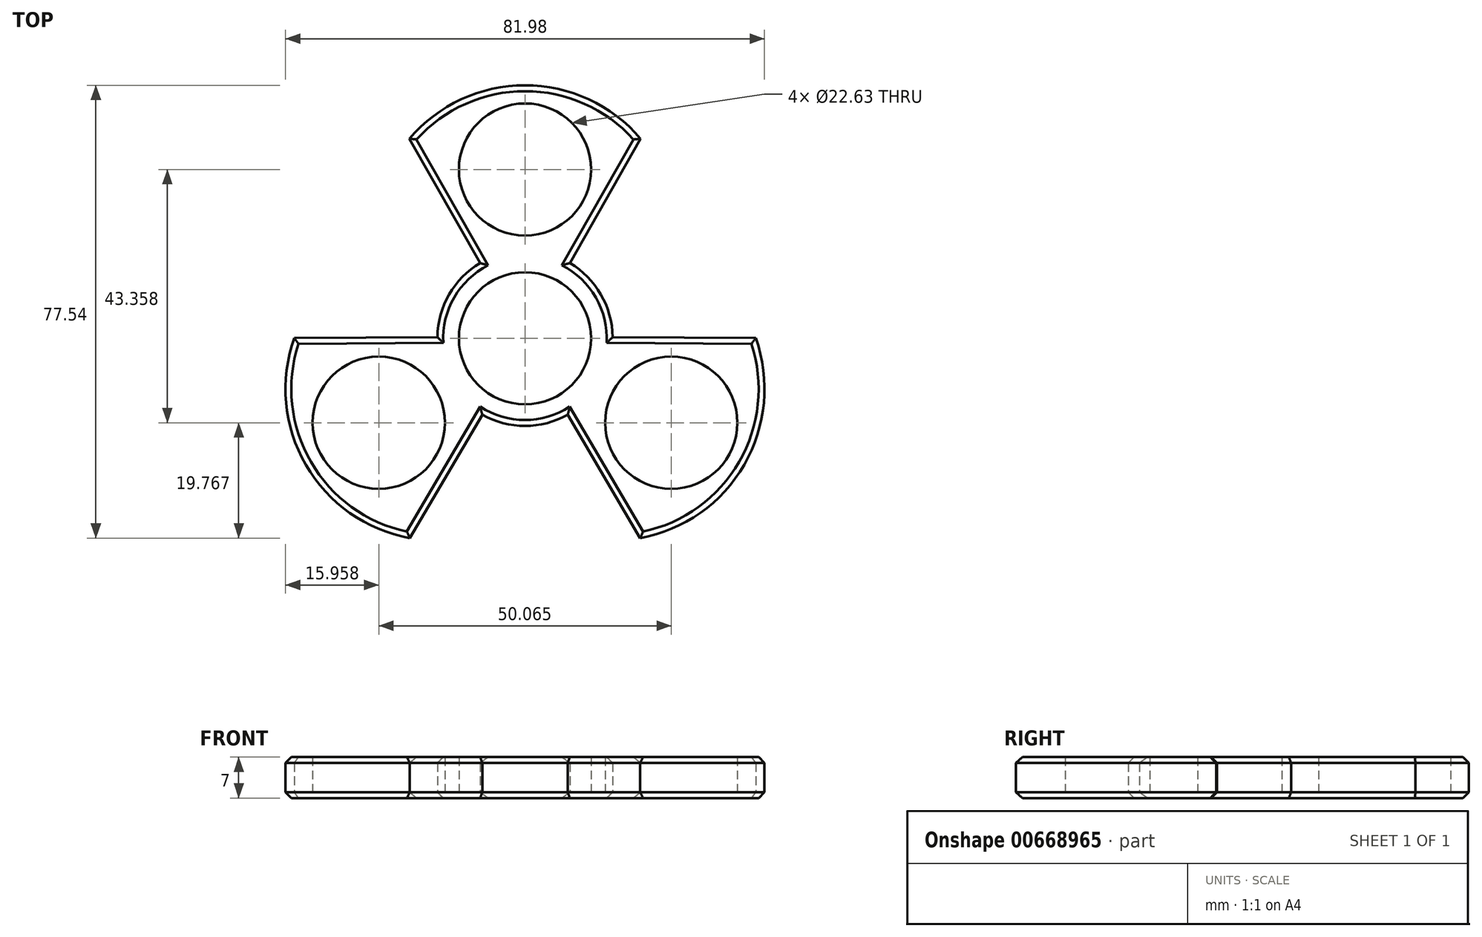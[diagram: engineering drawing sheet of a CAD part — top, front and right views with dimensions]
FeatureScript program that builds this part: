
annotation { "Feature Type Name" : "Feature", "Feature Type Description" : "" }
export const myFeature = defineFeature(function(context is Context, id is Id, definition is map)
    precondition{}
    {
        {
            var Q0;
            Q0=qCreatedBy(makeId("Top.planeOp"),FACE);
            var sketch = newSketch(context, id + "F0", { "sketchPlane" : qUnion([Q0])});
            skCircle(sketch, "E0", {"center": v(0, 0) * mm, "radius": 11.32 * mm});
            skCircle(sketch, "E1", {"center": v(0, 0) * mm, "radius": 45 * mm, "construction": true});
            skCircle(sketch, "E2", {"center": v(0, 0) * mm, "radius": 15 * mm});
            skLineSegment(sketch, "E3", {"start": v(-7.69, 12.88) * mm, "end": v(-19.78, 34.18) * mm});
            skLineSegment(sketch, "E4.MirrorCS", {"start": v(7.69, 12.88) * mm, "end": v(19.78, 34.18) * mm});
            skArc(sketch, "E5", {"start": v(19.78, 34.18) * mm, "mid": v(0, 43.32) * mm, "end": v(-19.78, 34.18) * mm});
            skCircle(sketch, "E6", {"center": v(0, 28.9) * mm, "radius": 11.32 * mm});
            skLineSegment(sketch, "E7.1.0", {"start": v(-7.31, -13.1) * mm, "end": v(-19.7, -34.22) * mm});
            skArc(sketch, "E7.1.1", {"start": v(-39.49, 0.05) * mm, "mid": v(-37.51, -21.66) * mm, "end": v(-19.7, -34.22) * mm});
            skCircle(sketch, "E7.1.2", {"center": v(-25.03, -14.45) * mm, "radius": 11.32 * mm});
            skLineSegment(sketch, "E7.1.3", {"start": v(-15, 0.22) * mm, "end": v(-39.49, 0.05) * mm});
            skLineSegment(sketch, "E7.2.0", {"start": v(15, 0.22) * mm, "end": v(39.49, 0.05) * mm});
            skArc(sketch, "E7.2.1", {"start": v(19.7, -34.22) * mm, "mid": v(37.51, -21.66) * mm, "end": v(39.49, 0.05) * mm});
            skCircle(sketch, "E7.2.2", {"center": v(25.03, -14.45) * mm, "radius": 11.32 * mm});
            skLineSegment(sketch, "E7.2.3", {"start": v(7.31, -13.1) * mm, "end": v(19.7, -34.22) * mm});
            skSolve(sketch);
        }
        {
            var Q0;
            Q0 = qSketchRegion(id + "F0", true);
            extrude(context, id + "F1", {"entities" : qUnion([Q0]), "depth" : 7 * mm, "offsetDistance" : 25 * mm});
        }
        {
            var Q0;
            Q0=makeQuery(id+"F1.opExtrude","CAP_EDGE",EDGE,{"disambiguationData":[OSD([sQuery(id+"F0.wireOp",EDGE,"E7.1.3")])],"isStart":false});
            var Q1;
            Q1=makeQuery(id+"F1.opExtrude","CAP_EDGE",EDGE,{"disambiguationData":[OSD([sQuery(id+"F0.wireOp",EDGE,"E3")])],"isStart":false});
            var Q2;
            Q2=makeQuery(id+"F1.opExtrude","CAP_EDGE",EDGE,{"disambiguationData":[OSD([sQuery(id+"F0.wireOp",EDGE,"E7.2.0")])],"isStart":false});
            var Q3;
            Q3=makeQuery(id+"F1.opExtrude","CAP_EDGE",EDGE,{"disambiguationData":[OSD([sQuery(id+"F0.wireOp",EDGE,"E4.MirrorCS")])],"isStart":false});
            var Q4;
            Q4=makeQuery(id+"F1.opExtrude","CAP_EDGE",EDGE,{"disambiguationData":[OSD([sQuery(id+"F0.wireOp",EDGE,"E7.2.3")])],"isStart":false});
            var Q5;
            Q5=makeQuery(id+"F1.opExtrude","CAP_EDGE",EDGE,{"disambiguationData":[OSD([sQuery(id+"F0.wireOp",EDGE,"E7.1.0")])],"isStart":false});
            var Q6;
            Q6=makeQuery(id+"F1.opExtrude","CAP_EDGE",EDGE,{"disambiguationData":[OSD([sQuery(id+"F0.wireOp",EDGE,"E7.1.1")])],"isStart":false});
            var Q7;
            Q7=makeQuery(id+"F1.opExtrude","CAP_EDGE",EDGE,{"disambiguationData":[OSD([sQuery(id+"F0.wireOp",EDGE,"E7.2.1")])],"isStart":false});
            var Q8;
            Q8=makeQuery(id+"F1.opExtrude","CAP_EDGE",EDGE,{"disambiguationData":[OSD([sQuery(id+"F0.wireOp",EDGE,"E5")])],"isStart":false});
            var Q9;
            {var subQ0=sQuery(id+"F0.wireOp",EDGE,"E2");Q9=makeQuery(id+"F1.opExtrude","CAP_EDGE",EDGE,{"disambiguationData":[OSD([subQ0]),TDD([makeQuery(id+"F0.imprint","IMPRINT",EDGE,{"disambiguationData":[TD([[makeQuery(id+"F0.imprint","INTERSECT",VERTEX,{"derivedFrom":[subQ0,sQuery(id+"F0.wireOp",EDGE,"E3")]}),-1.0]])],"derivedFrom":subQ0})])],"isStart":false});}
            var Q10;
            {var subQ0=sQuery(id+"F0.wireOp",EDGE,"E2");Q10=makeQuery(id+"F1.opExtrude","CAP_EDGE",EDGE,{"disambiguationData":[OSD([subQ0]),TDD([makeQuery(id+"F0.imprint","IMPRINT",EDGE,{"disambiguationData":[TD([[makeQuery(id+"F0.imprint","INTERSECT",VERTEX,{"derivedFrom":[subQ0,sQuery(id+"F0.wireOp",EDGE,"E4.MirrorCS")]}),1.0]])],"derivedFrom":subQ0})])],"isStart":false});}
            var Q11;
            {var subQ0=sQuery(id+"F0.wireOp",EDGE,"E2");Q11=makeQuery(id+"F1.opExtrude","CAP_EDGE",EDGE,{"disambiguationData":[OSD([subQ0]),TDD([makeQuery(id+"F0.imprint","IMPRINT",EDGE,{"disambiguationData":[TD([[makeQuery(id+"F0.imprint","INTERSECT",VERTEX,{"derivedFrom":[subQ0,sQuery(id+"F0.wireOp",EDGE,"E7.1.0")]}),-1.0]])],"derivedFrom":subQ0})])],"isStart":false});}
            var Q12;
            {var subQ0=sQuery(id+"F0.wireOp",EDGE,"E2");Q12=makeQuery(id+"F1.opExtrude","CAP_EDGE",EDGE,{"disambiguationData":[OSD([subQ0]),TDD([makeQuery(id+"F0.imprint","IMPRINT",EDGE,{"disambiguationData":[TD([[makeQuery(id+"F0.imprint","INTERSECT",VERTEX,{"derivedFrom":[subQ0,sQuery(id+"F0.wireOp",EDGE,"E7.1.0")]}),-1.0]])],"derivedFrom":subQ0})])],"isStart":true});}
            var Q13;
            Q13=makeQuery(id+"F1.opExtrude","CAP_EDGE",EDGE,{"disambiguationData":[OSD([sQuery(id+"F0.wireOp",EDGE,"E7.2.3")])],"isStart":true});
            var Q14;
            Q14=makeQuery(id+"F1.opExtrude","CAP_EDGE",EDGE,{"disambiguationData":[OSD([sQuery(id+"F0.wireOp",EDGE,"E7.1.0")])],"isStart":true});
            var Q15;
            Q15=makeQuery(id+"F1.opExtrude","CAP_EDGE",EDGE,{"disambiguationData":[OSD([sQuery(id+"F0.wireOp",EDGE,"E7.2.1")])],"isStart":true});
            var Q16;
            Q16=makeQuery(id+"F1.opExtrude","CAP_EDGE",EDGE,{"disambiguationData":[OSD([sQuery(id+"F0.wireOp",EDGE,"E7.2.0")])],"isStart":true});
            var Q17;
            {var subQ0=sQuery(id+"F0.wireOp",EDGE,"E2");Q17=makeQuery(id+"F1.opExtrude","CAP_EDGE",EDGE,{"disambiguationData":[OSD([subQ0]),TDD([makeQuery(id+"F0.imprint","IMPRINT",EDGE,{"disambiguationData":[TD([[makeQuery(id+"F0.imprint","INTERSECT",VERTEX,{"derivedFrom":[subQ0,sQuery(id+"F0.wireOp",EDGE,"E4.MirrorCS")]}),1.0]])],"derivedFrom":subQ0})])],"isStart":true});}
            var Q18;
            Q18=makeQuery(id+"F1.opExtrude","CAP_EDGE",EDGE,{"disambiguationData":[OSD([sQuery(id+"F0.wireOp",EDGE,"E4.MirrorCS")])],"isStart":true});
            var Q19;
            Q19=makeQuery(id+"F1.opExtrude","CAP_EDGE",EDGE,{"disambiguationData":[OSD([sQuery(id+"F0.wireOp",EDGE,"E5")])],"isStart":true});
            var Q20;
            Q20=makeQuery(id+"F1.opExtrude","CAP_EDGE",EDGE,{"disambiguationData":[OSD([sQuery(id+"F0.wireOp",EDGE,"E3")])],"isStart":true});
            var Q21;
            {var subQ0=sQuery(id+"F0.wireOp",EDGE,"E2");Q21=makeQuery(id+"F1.opExtrude","CAP_EDGE",EDGE,{"disambiguationData":[OSD([subQ0]),TDD([makeQuery(id+"F0.imprint","IMPRINT",EDGE,{"disambiguationData":[TD([[makeQuery(id+"F0.imprint","INTERSECT",VERTEX,{"derivedFrom":[subQ0,sQuery(id+"F0.wireOp",EDGE,"E3")]}),-1.0]])],"derivedFrom":subQ0})])],"isStart":true});}
            var Q22;
            Q22=makeQuery(id+"F1.opExtrude","CAP_EDGE",EDGE,{"disambiguationData":[OSD([sQuery(id+"F0.wireOp",EDGE,"E7.1.3")])],"isStart":true});
            var Q23;
            Q23=makeQuery(id+"F1.opExtrude","CAP_EDGE",EDGE,{"disambiguationData":[OSD([sQuery(id+"F0.wireOp",EDGE,"E7.1.1")])],"isStart":true});
            chamfer(context, id + "F2", {"entities" : qUnion([Q0, Q1, Q2, Q3, Q4, Q5, Q6, Q7, Q8, Q9, Q10, Q11, Q12, Q13, Q14, Q15, Q16, Q17, Q18, Q19, Q20, Q21, Q22, Q23]), "width" : 1 * mm, "tangentPropagation" : true});
        }
    });
